# Revit family: xLIFE-PRO-SPOT_Non-Hosted_R16
name_source: partatom
category: Lighting Fixtures
revit_build: Autodesk Revit 2016 (Build: 20151007_0715(x64)
units: mm (PartAtom-declared; Revit-internal decimal feet)

## family parameters
Always vertical = Yes
Cut with Voids When Loaded = No
Light Source = Yes
OmniClass Number = 23.80.70.00
OmniClass Title = Lighting
Part Type = Normal
Room Calculation Point = No
Round Connector Dimension = Use Diameter
Shared = No
Work Plane-Based = No

## types (2) — shared parameters
Charging Method = Intelligent current limited constant voltage charger
Color Filter = 16777215
Dimensions (Control Pack) = 232mm x 40mm x 40mm (Control Pack)
Dimensions (Lamp Head and Swivel) = 105mm x 100mm x 60mm (Lamp Head and Swivel)
Dimming Lamp Color Temperature Shift = <None>
Emergency Lumen Output = 280lm
Emit Shape Visible in Rendering = No
IP Rating = IP20
Lamp = 2 x 3W LED (Lifetime warranty on the lamp head and loom assembly)
Manufacturer = Clevertronics
Mounting = Lamp head assembly - Ceiling or wall mount
Operating Mode = Non-Maintained
Operating Temperature = 1˚ to 40˚C (Ambient)
Operating Voltage = 240V 50Hz
Photometric Web File = ll15956 - LLIFEM-PRO-ZW.ies
Replacement Emergency Lamp = 1100830 Lamps: 2 x 3W LED Round Head Assembly - White
Testing System = Manual Test Switch
Tilt Angle = 90.00°

## per-type parameters (varying)
| type | AS2293 Classification | Battery | Description | MIC Number | Power Consumption | Power Consumption (Standby) | Product Description | Replacement Battery | Replacement Emergency Driver |
| LLIFE-PRO-SPOT | C0=D50 C90=D50 | 3.3V 5000mA Lithium Iron Nanophosphate | Lifelight Pro, LED, Surface,Spot,L10,OWC,Gen 2,D80 | AUT01310170001 | 2.2W | 0.4W | L10 Lifelight PRO, High Performance, Spotlight Style Emergency Light | 1530230 Battery: 3.3V 5Ah.Li-ion, 200mm lead with Bracket | LLIFE-PRO-CKIT PCA: Lifelight Pro Control Gear |
| CLIFE-PRO-SPOT |  | 3.2V 6400mA Lithium Iron | Lifelight PRO, High Performance, Recessed Emergency Spotlight with Lithium Battery Technology - Black | AUT02310200001 | 0.4W |  | Lifelight PRO, High Performance, Spotlight Style Emergency Light | 1550230 Battery, LP 3.2V 6400mAh.200mm lead.Brkt. | 8002390 Driver, PCA:Lifelight Pro, Zoneworks Compatible |

note: column(s) folded — value = type name in every type: Model

## geometry (parser evidence)
native form markers: Sweep x3
no freeform markers — native parametric forms only
